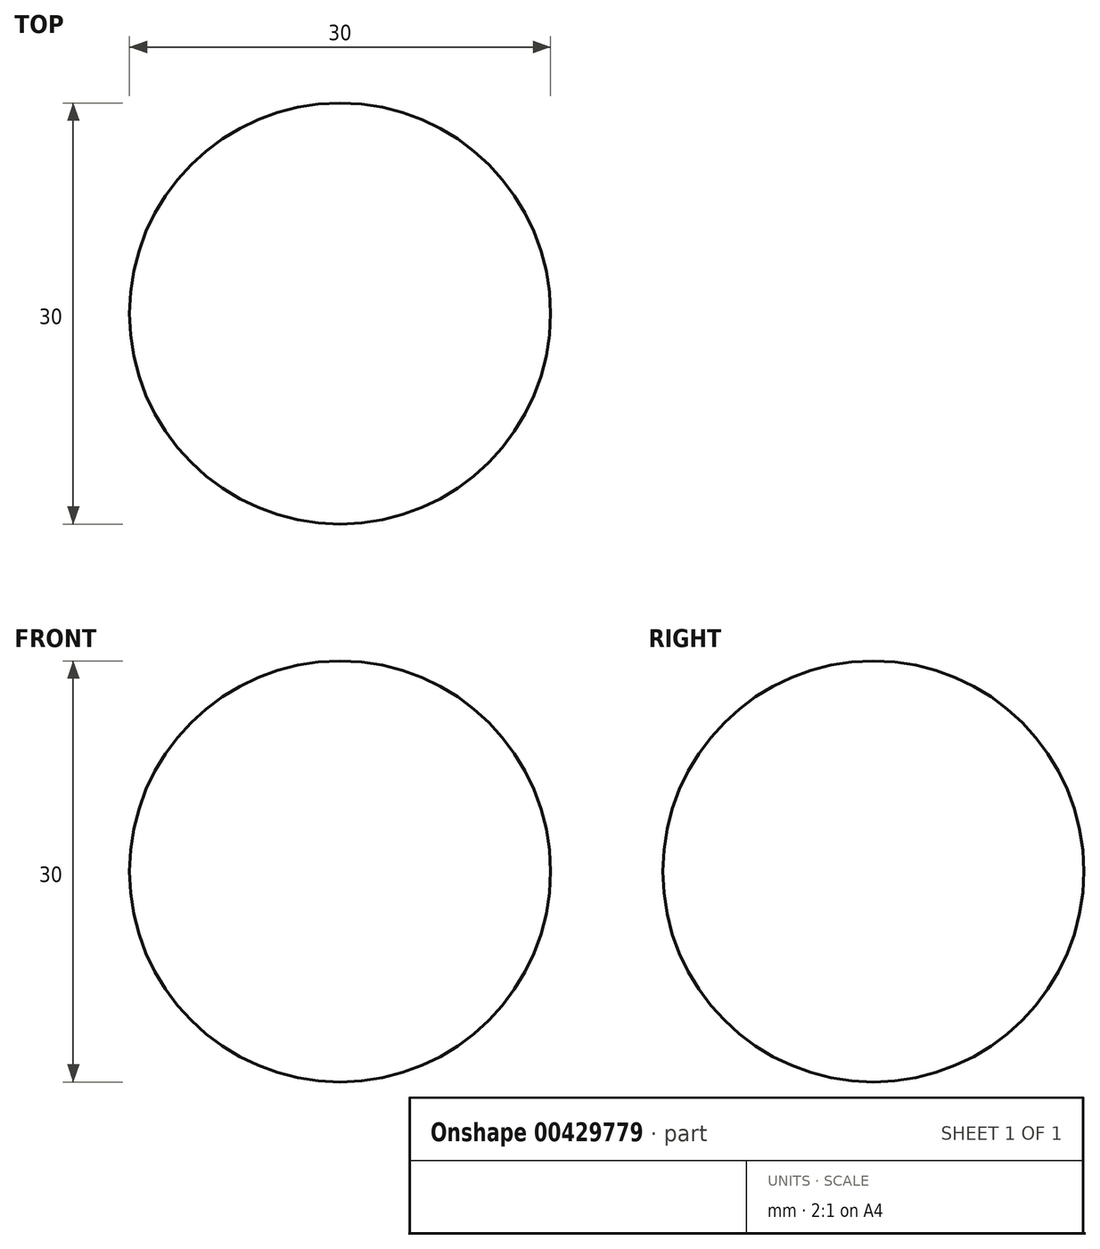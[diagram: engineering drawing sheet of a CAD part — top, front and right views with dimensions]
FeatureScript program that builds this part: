
annotation { "Feature Type Name" : "Feature", "Feature Type Description" : "" }
export const myFeature = defineFeature(function(context is Context, id is Id, definition is map)
    precondition{}
    {
        {
            var Q0;
            Q0=qCreatedBy(makeId("Top.planeOp"),FACE);
            var sketch = newSketch(context, id + "F0", { "sketchPlane" : qUnion([Q0])});
            skLineSegment(sketch, "E0", {"start": v(0, 0) * mm, "end": v(0, 30) * mm});
            skArc(sketch, "E1", {"start": v(0, 30) * mm, "mid": v(-15, 15) * mm, "end": v(0, 0) * mm});
            skSolve(sketch);
        }
        {
            var Q0;
            Q0=makeQuery(id+"F0.imprint","IMPRINT",FACE,{"disambiguationData":[TD([[makeQuery(id+"F0.imprint","IMPRINT",EDGE,{"derivedFrom":sQuery(id+"F0.wireOp",EDGE,"E0")}),1.0]])]});
            var Q1;
            Q1=sQuery(id+"F0.wireOp",EDGE,"E1");
            var Q2;
            Q2=sQuery(id+"F0.wireOp",EDGE,"E0");
            revolve(context, id + "F1", {"entities" : qUnion([Q0]), "surfaceEntities" : qUnion([Q1]), "axis" : qUnion([Q2]), "revolveType" : RevolveType.FULL});
        }
    });
